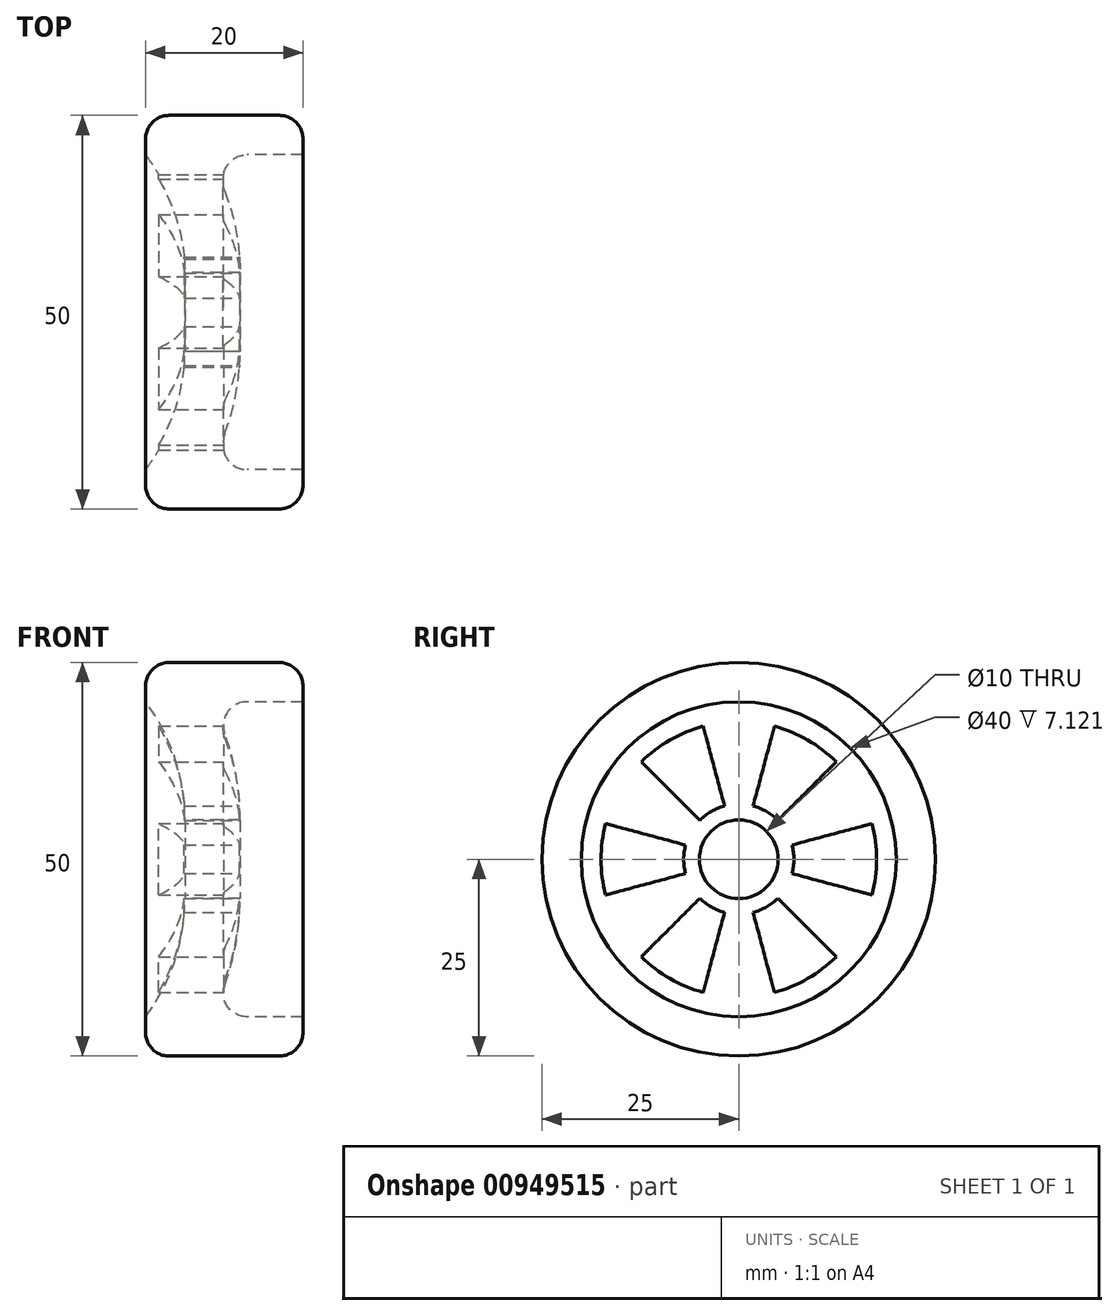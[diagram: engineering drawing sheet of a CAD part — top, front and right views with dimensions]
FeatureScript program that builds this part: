
annotation { "Feature Type Name" : "Feature", "Feature Type Description" : "" }
export const myFeature = defineFeature(function(context is Context, id is Id, definition is map)
    precondition{}
    {
        {
            var Q0;
            Q0=qCreatedBy(makeId("Front.planeOp"),FACE);
            var sketch = newSketch(context, id + "F0", { "sketchPlane" : qUnion([Q0])});
            skLineSegment(sketch, "E0.top", {"start": v(-3, 25) * mm, "end": v(-17, 25) * mm});
            skLineSegment(sketch, "E1", {"start": v(-20, 22) * mm, "end": v(-20, 20) * mm});
            skLineSegment(sketch, "E2", {"start": v(-14, 0) * mm, "end": v(0, 0) * mm});
            skLineSegment(sketch, "E3", {"start": v(0, 22) * mm, "end": v(0, 20) * mm});
            skArc(sketch, "E4", {"start": v(-15, 5) * mm, "mid": v(-16.28, 12.9) * mm, "end": v(-20, 20) * mm});
            skArc(sketch, "E5.0", {"start": v(-8, 5) * mm, "mid": v(-8.49, 10.57) * mm, "end": v(-9.94, 15.97) * mm});
            skLineSegment(sketch, "E6", {"start": v(-8, 5) * mm, "end": v(-8, 0) * mm});
            skLineSegment(sketch, "E7", {"start": v(0, 20) * mm, "end": v(-7.12, 20) * mm});
            skPoint(sketch, "E8.visualSharp", {"position": v(-11.73, 20) * mm});
            skArc(sketch, "E8.filletArc", {"start": v(-7.12, 20) * mm, "mid": v(-9.58, 18.72) * mm, "end": v(-9.94, 15.97) * mm});
            skLineSegment(sketch, "E9", {"start": v(-15, 5) * mm, "end": v(-14, 5) * mm});
            skLineSegment(sketch, "E10", {"start": v(-14, 5) * mm, "end": v(-14, 0) * mm});
            skPoint(sketch, "E11.visualSharp", {"position": v(-20, 25) * mm});
            skArc(sketch, "E11.filletArc", {"start": v(-17, 25) * mm, "mid": v(-19.12, 24.12) * mm, "end": v(-20, 22) * mm});
            skPoint(sketch, "E12.visualSharp", {"position": v(0, 25) * mm});
            skArc(sketch, "E12.filletArc", {"start": v(0, 22) * mm, "mid": v(-0.88, 24.12) * mm, "end": v(-3, 25) * mm});
            skSolve(sketch);
        }
        {
            var Q0;
            Q0=makeQuery(id+"F0.imprint","IMPRINT",FACE,{"disambiguationData":[TD([[makeQuery(id+"F0.imprint","IMPRINT",EDGE,{"derivedFrom":sQuery(id+"F0.wireOp",EDGE,"E0.top")}),1.0]])]});
            var Q1;
            Q1=sQuery(id+"F0.wireOp",EDGE,"E2");
            revolve(context, id + "F1", {"surfaceOperationType" : NewSurfaceOperationType.NEW, "entities" : qUnion([Q0]), "axis" : qUnion([Q1]), "revolveType" : RevolveType.FULL});
        }
        {
            var Q0;
            Q0=qCreatedBy(makeId("Right.planeOp"),FACE);
            var sketch = newSketch(context, id + "F2", { "sketchPlane" : qUnion([Q0])});
            skArc(sketch, "E13", {"start": v(-16.9, 4.53) * mm, "mid": v(-17.5, 0) * mm, "end": v(-16.9, -4.53) * mm});
            skArc(sketch, "E14", {"start": v(-6.76, 1.81) * mm, "mid": v(-7, 0) * mm, "end": v(-6.76, -1.81) * mm});
            skLineSegment(sketch, "E15", {"start": v(-6.76, 1.81) * mm, "end": v(-16.9, 4.53) * mm});
            skLineSegment(sketch, "E16", {"start": v(-6.76, -1.81) * mm, "end": v(-16.9, -4.53) * mm});
            skLineSegment(sketch, "E17.1.0", {"start": v(-4.95, -4.95) * mm, "end": v(-12.37, -12.37) * mm});
            skArc(sketch, "E17.1.1", {"start": v(-4.95, -4.95) * mm, "mid": v(-3.5, -6.06) * mm, "end": v(-1.81, -6.76) * mm});
            skLineSegment(sketch, "E17.1.2", {"start": v(-1.81, -6.76) * mm, "end": v(-4.53, -16.9) * mm});
            skArc(sketch, "E17.1.3", {"start": v(-12.37, -12.37) * mm, "mid": v(-8.75, -15.16) * mm, "end": v(-4.53, -16.9) * mm});
            skLineSegment(sketch, "E17.2.0", {"start": v(1.81, -6.76) * mm, "end": v(4.53, -16.9) * mm});
            skArc(sketch, "E17.2.1", {"start": v(1.81, -6.76) * mm, "mid": v(3.5, -6.06) * mm, "end": v(4.95, -4.95) * mm});
            skLineSegment(sketch, "E17.2.2", {"start": v(4.95, -4.95) * mm, "end": v(12.37, -12.37) * mm});
            skArc(sketch, "E17.2.3", {"start": v(4.53, -16.9) * mm, "mid": v(8.75, -15.16) * mm, "end": v(12.37, -12.37) * mm});
            skLineSegment(sketch, "E17.3.0", {"start": v(6.76, -1.81) * mm, "end": v(16.9, -4.53) * mm});
            skArc(sketch, "E17.3.1", {"start": v(6.76, -1.81) * mm, "mid": v(7, 0) * mm, "end": v(6.76, 1.81) * mm});
            skLineSegment(sketch, "E17.3.2", {"start": v(6.76, 1.81) * mm, "end": v(16.9, 4.53) * mm});
            skArc(sketch, "E17.3.3", {"start": v(16.9, -4.53) * mm, "mid": v(17.5, 0) * mm, "end": v(16.9, 4.53) * mm});
            skLineSegment(sketch, "E17.4.0", {"start": v(4.95, 4.95) * mm, "end": v(12.37, 12.37) * mm});
            skArc(sketch, "E17.4.1", {"start": v(4.95, 4.95) * mm, "mid": v(3.5, 6.06) * mm, "end": v(1.81, 6.76) * mm});
            skLineSegment(sketch, "E17.4.2", {"start": v(1.81, 6.76) * mm, "end": v(4.53, 16.9) * mm});
            skArc(sketch, "E17.4.3", {"start": v(12.37, 12.37) * mm, "mid": v(8.75, 15.16) * mm, "end": v(4.53, 16.9) * mm});
            skLineSegment(sketch, "E17.5.0", {"start": v(-1.81, 6.76) * mm, "end": v(-4.53, 16.9) * mm});
            skArc(sketch, "E17.5.1", {"start": v(-1.81, 6.76) * mm, "mid": v(-3.5, 6.06) * mm, "end": v(-4.95, 4.95) * mm});
            skLineSegment(sketch, "E17.5.2", {"start": v(-4.95, 4.95) * mm, "end": v(-12.37, 12.37) * mm});
            skArc(sketch, "E17.5.3", {"start": v(-4.53, 16.9) * mm, "mid": v(-8.75, 15.16) * mm, "end": v(-12.37, 12.37) * mm});
            skSolve(sketch);
        }
        {
            var Q0;
            {var subQ0=sQuery(id+"F2.wireOp",EDGE,"E15");var subQ1=sQuery(id+"F2.wireOp",EDGE,"E13");var subQ2=makeQuery(id+"F2.imprint","INTERSECT",VERTEX,{"derivedFrom":[subQ1,subQ0]});Q0=makeQuery(id+"F2.imprint","IMPRINT",FACE,{"disambiguationData":[TD([[makeQuery(id+"F2.imprint","IMPRINT",EDGE,{"disambiguationData":[TD([[subQ2,-1.0]])],"derivedFrom":subQ1}),1.0]])]});}
            var Q1;
            Q1=makeQuery(id+"F2.imprint","IMPRINT",FACE,{"disambiguationData":[TD([[makeQuery(id+"F2.imprint","IMPRINT",EDGE,{"derivedFrom":sQuery(id+"F2.wireOp",EDGE,"E17.5.0")}),1.0]])]});
            var Q2;
            Q2=makeQuery(id+"F2.imprint","IMPRINT",FACE,{"disambiguationData":[TD([[makeQuery(id+"F2.imprint","IMPRINT",EDGE,{"derivedFrom":sQuery(id+"F2.wireOp",EDGE,"E17.4.0")}),1.0]])]});
            var Q3;
            Q3=makeQuery(id+"F2.imprint","IMPRINT",FACE,{"disambiguationData":[TD([[makeQuery(id+"F2.imprint","IMPRINT",EDGE,{"derivedFrom":sQuery(id+"F2.wireOp",EDGE,"E17.3.0")}),1.0]])]});
            var Q4;
            Q4=makeQuery(id+"F2.imprint","IMPRINT",FACE,{"disambiguationData":[TD([[makeQuery(id+"F2.imprint","IMPRINT",EDGE,{"derivedFrom":sQuery(id+"F2.wireOp",EDGE,"E17.2.0")}),1.0]])]});
            var Q5;
            Q5=makeQuery(id+"F2.imprint","IMPRINT",FACE,{"disambiguationData":[TD([[makeQuery(id+"F2.imprint","IMPRINT",EDGE,{"derivedFrom":sQuery(id+"F2.wireOp",EDGE,"E17.1.0")}),1.0]])]});
            extrude(context, id + "F3", {"entities" : qUnion([Q0, Q1, Q2, Q3, Q4, Q5]), "operationType" : NewBodyOperationType.REMOVE, "oppositeDirection" : true, "depth" : 25 * mm, "offsetDistance" : 25 * mm});
        }
        {
            var Q0;
            Q0=qCreatedBy(makeId("Right.planeOp"),FACE);
            var sketch = newSketch(context, id + "F4", { "sketchPlane" : qUnion([Q0])});
            skCircle(sketch, "E18", {"center": v(0, 0) * mm, "radius": 5 * mm});
            skSolve(sketch);
        }
        {
            var Q0;
            Q0=makeQuery(id+"F4.imprint","IMPRINT",FACE,{"disambiguationData":[TD([[makeQuery(id+"F4.imprint","IMPRINT",EDGE,{"derivedFrom":sQuery(id+"F4.wireOp",EDGE,"E18")}),1.0]])]});
            extrude(context, id + "F5", {"entities" : qUnion([Q0]), "operationType" : NewBodyOperationType.REMOVE, "oppositeDirection" : true, "depth" : 25 * mm, "offsetDistance" : 25 * mm});
        }
    });
